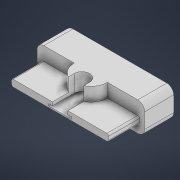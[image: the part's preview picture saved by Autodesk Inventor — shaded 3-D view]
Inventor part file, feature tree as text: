
AUTODESK INVENTOR PART (.ipt)
format: ipt  version: 2022 (Build 260153000, 153)  size: 471,552 bytes
history: native  units: mm
features: sketch x7, extrude x6, fillet x2, emboss x1
ambient origin geometry x8: Origin, YZ Plane, XZ Plane, XY Plane, X Axis, Y Axis, Z Axis, Center Point
bodies: Solid1 (feature_tree)
feature tree (16):
  extrude  "Extrusion1"  Depth=17.0mm
  emboss  "Emboss1"
  extrude  "Extrusion12"  Depth=1.0mm TaperAngle=0.0deg
  extrude  "Extrusion13"  Depth=8.0mm
  extrude  "Extrusion14"  Depth=18.0mm TaperAngle=0.0deg
  extrude  "Extrusion15"  Depth=56.8mm
  fillet  "Fillet6"  Radius=18.0mm
  fillet  "Fillet7"  Radius=1.0mm
  extrude  "Extrusion16"  Depth=4.0mm
  sketch  "Sketch1"  dims[d0=63.0mm d1=17.0mm]
  sketch  "Sketch10"  dims[d2=35.0mm d3=0.0mm d33=1.0mm d34=0.0mm]
  sketch  "Sketch15"  dims[d67=5.0mm d68=8.0mm]
  sketch  "Sketch16"  dims[d69=18.0mm d70=0.0mm d73=2.0mm d74=0.0mm]
  sketch  "Sketch17"  dims[d76=1.2mm d77=0.0mm d78=56.8mm d79=18.0mm d80=0.0mm d81=1.0mm]
  sketch  "Sketch18"  dims[d82=4.0mm d84=19.5mm]
  sketch  "Sketch19"  dims[d85=8.0mm d86=0.0mm d88=12.75mm d89=9.0mm d90=13.4mm d51=0.5mm d52=0.872665mm d53=0.5mm d54=0.872665mm]
